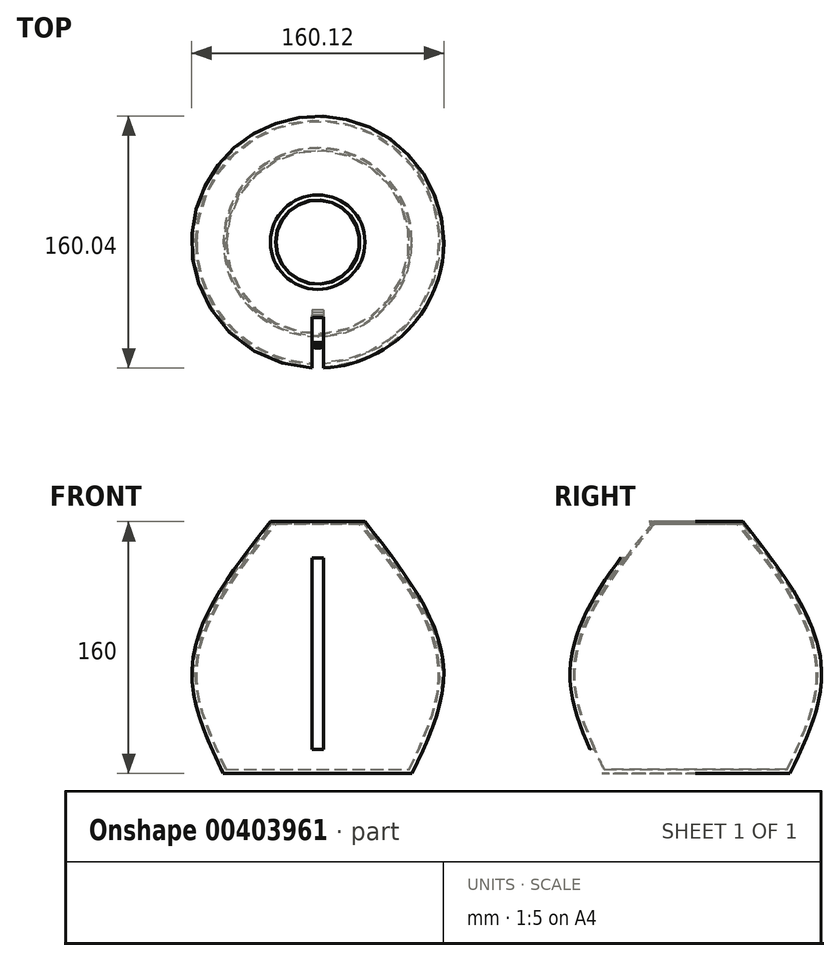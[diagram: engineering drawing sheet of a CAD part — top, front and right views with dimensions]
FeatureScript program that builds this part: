
annotation { "Feature Type Name" : "Feature", "Feature Type Description" : "" }
export const myFeature = defineFeature(function(context is Context, id is Id, definition is map)
    precondition{}
    {
        {
            var Q0;
            Q0=qCreatedBy(makeId("Top.planeOp"),FACE);
            var sketch = newSketch(context, id + "F0", { "sketchPlane" : qUnion([Q0])});
            skCircle(sketch, "E0", {"center": v(0, 0) * mm, "radius": 60 * mm});
            skSolve(sketch);
        }
        {
            var Q0;
            Q0=qCreatedBy(makeId("Top.planeOp"),FACE);
            cPlane(context, id + "F1", {"entities" : qUnion([Q0]), "cplaneType" : CPlaneType.OFFSET, "offset" : 60 * mm, "width" : 150 * mm, "height" : 150 * mm});
        }
        {
            var Q0;
            Q0=qCreatedBy(id+"F1.planeOp",FACE);
            var sketch = newSketch(context, id + "F2", { "sketchPlane" : qUnion([Q0])});
            skCircle(sketch, "E1", {"center": v(0, 0) * mm, "radius": 80 * mm});
            skSolve(sketch);
        }
        {
            var Q0;
            Q0=qCreatedBy(id+"F1.planeOp",FACE);
            cPlane(context, id + "F3", {"entities" : qUnion([Q0]), "cplaneType" : CPlaneType.OFFSET, "offset" : 100 * mm, "width" : 150 * mm, "height" : 150 * mm});
        }
        {
            var Q0;
            Q0=qCreatedBy(id+"F3.planeOp",FACE);
            var sketch = newSketch(context, id + "F4", { "sketchPlane" : qUnion([Q0])});
            skCircle(sketch, "E2", {"center": v(0, 0) * mm, "radius": 30 * mm});
            skSolve(sketch);
        }
        {
            var Q0;
            Q0=makeQuery(id+"F0.imprint","IMPRINT",FACE,{"disambiguationData":[TD([[makeQuery(id+"F0.imprint","IMPRINT",EDGE,{"derivedFrom":sQuery(id+"F0.wireOp",EDGE,"E0")}),1.0]])]});
            var Q1;
            Q1=makeQuery(id+"F2.imprint","IMPRINT",FACE,{"disambiguationData":[TD([[makeQuery(id+"F2.imprint","IMPRINT",EDGE,{"derivedFrom":sQuery(id+"F2.wireOp",EDGE,"E1")}),1.0]])]});
            var Q2;
            Q2=makeQuery(id+"F4.imprint","IMPRINT",FACE,{"disambiguationData":[TD([[makeQuery(id+"F4.imprint","IMPRINT",EDGE,{"derivedFrom":sQuery(id+"F4.wireOp",EDGE,"E2")}),1.0]])]});
            loft(context, id + "F5", {"sheetProfilesArray" : [{ "sheetProfileEntities" : qUnion([Q0]) }, { "sheetProfileEntities" : qUnion([Q1]) }, { "sheetProfileEntities" : qUnion([Q2]) }]});
        }
        {
            var Q0;
            Q0=makeQuery(id+"F5.opLoft","CAP_FACE",FACE,{"disambiguationData":[OSD([makeQuery(id+"F4.imprint","IMPRINT",FACE,{"disambiguationData":[TD([[makeQuery(id+"F4.imprint","IMPRINT",EDGE,{"derivedFrom":sQuery(id+"F4.wireOp",EDGE,"E2")}),1.0]])]})])],"isStart":true});
            shell(context, id + "F6", {"entities" : qUnion([Q0]), "thickness" : 2.5 * mm});
        }
        {
            var Q0;
            Q0=qCreatedBy(makeId("Front.planeOp"),FACE);
            cPlane(context, id + "F7", {"entities" : qUnion([Q0]), "cplaneType" : CPlaneType.OFFSET, "offset" : 86 * mm, "width" : 150 * mm, "height" : 150 * mm});
        }
        {
            var Q0;
            Q0=makeQuery(id+"F5.opLoft","SWEPT_BODY",BODY,{"disambiguationData":[OSD([makeQuery(id+"F0.imprint","IMPRINT",FACE,{"disambiguationData":[TD([[makeQuery(id+"F0.imprint","IMPRINT",EDGE,{"derivedFrom":sQuery(id+"F0.wireOp",EDGE,"E0")}),1.0]])]}),sQuery(id+"F2.wireOp",EDGE,"E1"),makeQuery(id+"F4.imprint","IMPRINT",FACE,{"disambiguationData":[TD([[makeQuery(id+"F4.imprint","IMPRINT",EDGE,{"derivedFrom":sQuery(id+"F4.wireOp",EDGE,"E2")}),1.0]])]})])]});
            var Q1;
            Q1=qCreatedBy(makeId("Origin.pointOp"),VERTEX);
            transform(context, id + "F8", {"entities" : qUnion([Q0]), "transformType" : TransformType.SCALE_UNIFORMLY, "scale" : 0.99, "scalePoint" : qUnion([Q1]), "makeCopy" : true});
        }
        {
            var Q0;
            Q0=qCreatedBy(makeId("Front.planeOp"),FACE);
            var sketch = newSketch(context, id + "F9", { "sketchPlane" : qUnion([Q0])});
            skLineSegment(sketch, "E3", {"start": v(0, 0) * mm, "end": v(0, 160.4) * mm, "construction": true});
            skSolve(sketch);
        }
        {
            var Q0;
            Q0=qCreatedBy(id+"F7.planeOp",FACE);
            var sketch = newSketch(context, id + "F10", { "sketchPlane" : qUnion([Q0])});
            skLineSegment(sketch, "E4", {"start": v(0, 15.34) * mm, "end": v(3.6, 15.34) * mm});
            skLineSegment(sketch, "E5", {"start": v(3.6, 15.34) * mm, "end": v(3.6, 136.85) * mm});
            skLineSegment(sketch, "E6", {"start": v(3.6, 136.85) * mm, "end": v(0, 136.85) * mm});
            skLineSegment(sketch, "E7.MirrorCS", {"start": v(-3.6, 136.85) * mm, "end": v(0, 136.85) * mm});
            skLineSegment(sketch, "E8.MirrorCS", {"start": v(-3.6, 15.34) * mm, "end": v(-3.6, 136.85) * mm});
            skLineSegment(sketch, "E9.MirrorCS", {"start": v(0, 15.34) * mm, "end": v(-3.6, 15.34) * mm});
            skSolve(sketch);
        }
        {
            var Q0;
            Q0=makeQuery(id+"F10.imprint","IMPRINT",FACE,{"disambiguationData":[TD([[makeQuery(id+"F10.imprint","IMPRINT",EDGE,{"derivedFrom":sQuery(id+"F10.wireOp",EDGE,"E4")}),1.0]])]});
            extrude(context, id + "F11", {"entities" : qUnion([Q0]), "operationType" : NewBodyOperationType.REMOVE, "oppositeDirection" : true, "depth" : 53 * mm});
        }
    });
